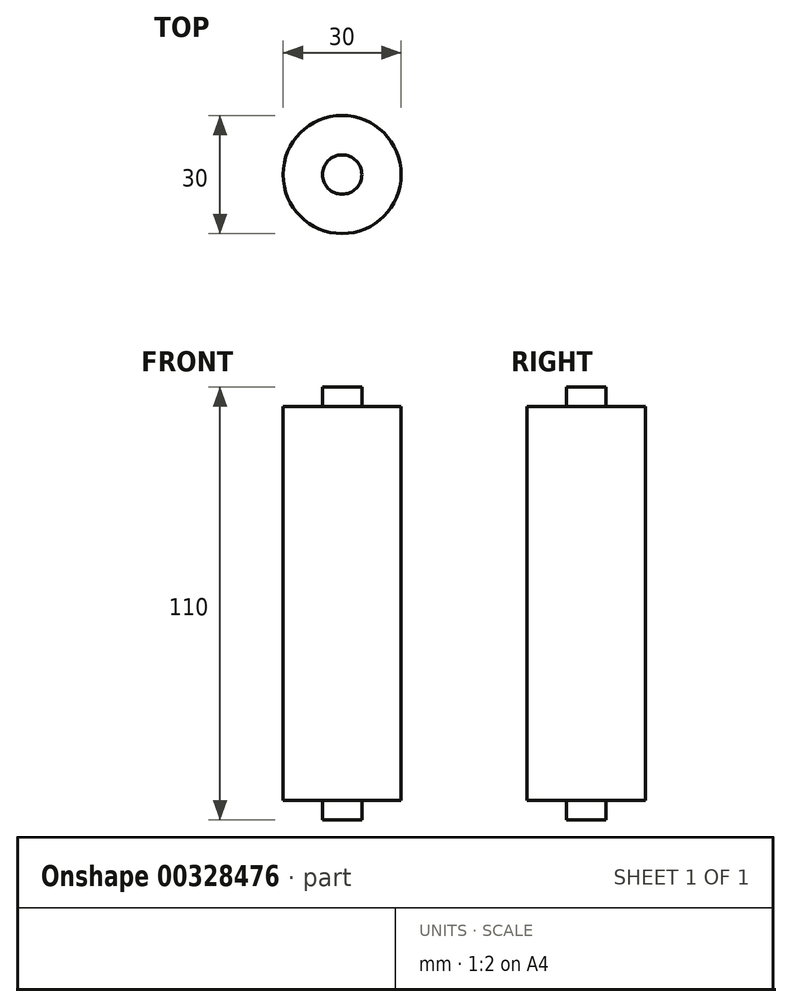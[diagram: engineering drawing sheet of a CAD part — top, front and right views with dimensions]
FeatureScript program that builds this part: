
annotation { "Feature Type Name" : "Feature", "Feature Type Description" : "" }
export const myFeature = defineFeature(function(context is Context, id is Id, definition is map)
    precondition{}
    {
        {
            var Q0;
            Q0=qCreatedBy(makeId("Top.planeOp"),FACE);
            var sketch = newSketch(context, id + "F0", { "sketchPlane" : qUnion([Q0])});
            skCircle(sketch, "E0", {"center": v(0, 0) * mm, "radius": 15 * mm});
            skSolve(sketch);
        }
        {
            var Q0;
            Q0 = qSketchRegion(id + "F0", true);
            extrude(context, id + "F1", {"entities" : qUnion([Q0]), "depth" : 100 * mm});
        }
        {
            var Q0;
            Q0=makeQuery(id+"F1.opExtrude","CAP_FACE",FACE,{"disambiguationData":[OSD([sQuery(id+"F0.wireOp",EDGE,"E0")])],"isStart":false});
            var sketch = newSketch(context, id + "F2", { "sketchPlane" : qUnion([Q0])});
            skCircle(sketch, "E1", {"center": v(0, 0) * mm, "radius": 5 * mm});
            skSolve(sketch);
        }
        {
            var Q0;
            Q0=makeQuery(id+"F2.imprint","IMPRINT",FACE,{"disambiguationData":[TD([[makeQuery(id+"F2.imprint","IMPRINT",EDGE,{"derivedFrom":sQuery(id+"F2.wireOp",EDGE,"E1")}),1.0]])]});
            extrude(context, id + "F3", {"entities" : qUnion([Q0]), "operationType" : NewBodyOperationType.ADD, "depth" : 5 * mm});
        }
        {
            var Q0;
            Q0=makeQuery(id+"F1.opExtrude","CAP_FACE",FACE,{"disambiguationData":[OSD([sQuery(id+"F0.wireOp",EDGE,"E0")])],"isStart":true});
            var sketch = newSketch(context, id + "F4", { "sketchPlane" : qUnion([Q0])});
            skCircle(sketch, "E2", {"center": v(0, 0) * mm, "radius": 5 * mm});
            skSolve(sketch);
        }
        {
            var Q0;
            Q0 = qSketchRegion(id + "F4", true);
            extrude(context, id + "F5", {"entities" : qUnion([Q0]), "operationType" : NewBodyOperationType.ADD, "depth" : 5 * mm});
        }
    });
